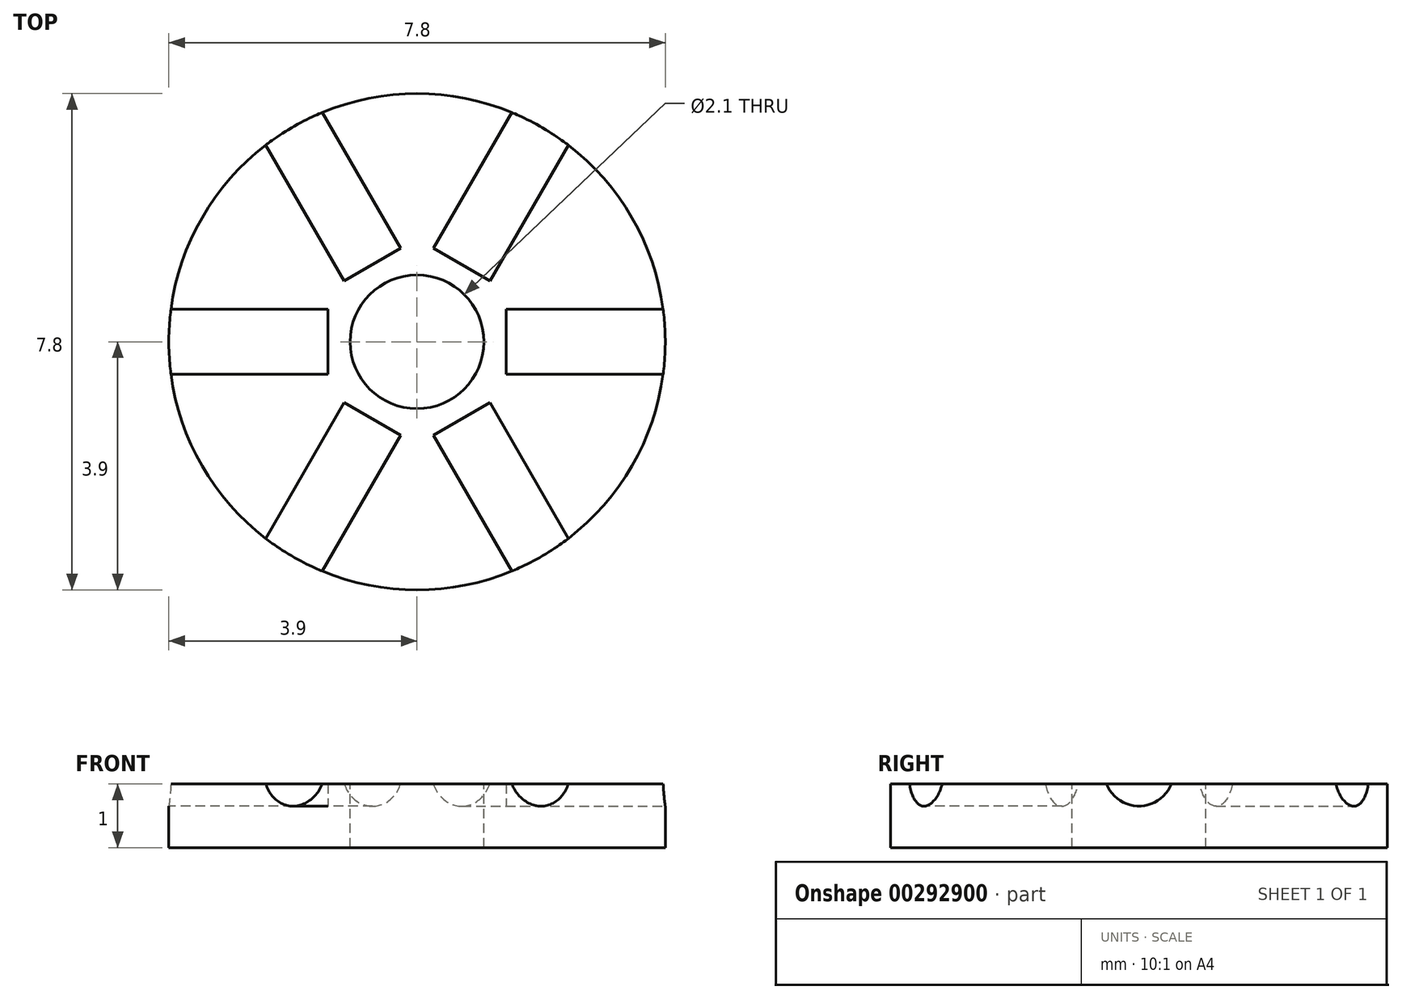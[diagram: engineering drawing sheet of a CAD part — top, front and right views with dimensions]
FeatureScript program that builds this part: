
annotation { "Feature Type Name" : "Feature", "Feature Type Description" : "" }
export const myFeature = defineFeature(function(context is Context, id is Id, definition is map)
    precondition{}
    {
        {
            var Q0;
            Q0=qCreatedBy(makeId("Top.planeOp"),FACE);
            var sketch = newSketch(context, id + "F0", { "sketchPlane" : qUnion([Q0])});
            skCircle(sketch, "E0", {"center": v(0, 0) * mm, "radius": 3.9 * mm});
            skSolve(sketch);
        }
        {
            var Q0;
            Q0=makeQuery(id+"F0.imprint","IMPRINT",FACE,{"disambiguationData":[TD([[makeQuery(id+"F0.imprint","IMPRINT",EDGE,{"derivedFrom":sQuery(id+"F0.wireOp",EDGE,"E0")}),1.0]])]});
            extrude(context, id + "F1", {"entities" : qUnion([Q0]), "depth" : 1 * mm});
        }
        {
            var Q0;
            Q0=makeQuery(id+"F1.opExtrude","CAP_FACE",FACE,{"disambiguationData":[OSD([sQuery(id+"F0.wireOp",EDGE,"E0")])],"isStart":false});
            var sketch = newSketch(context, id + "F2", { "sketchPlane" : qUnion([Q0])});
            skCircle(sketch, "E1", {"center": v(0, 0) * mm, "radius": 1.05 * mm});
            skSolve(sketch);
        }
        {
            var Q0;
            Q0=makeQuery(id+"F2.imprint","IMPRINT",FACE,{"disambiguationData":[TD([[makeQuery(id+"F2.imprint","IMPRINT",EDGE,{"derivedFrom":sQuery(id+"F2.wireOp",EDGE,"E1")}),1.0]])]});
            var Q1;
            Q1=sQuery(id+"F2.wireOp",EDGE,"E1");
            extrude(context, id + "F3", {"entities" : qUnion([Q0]), "operationType" : NewBodyOperationType.REMOVE, "surfaceEntities" : qUnion([Q1]), "oppositeDirection" : true, "depth" : 25 * mm});
        }
        {
            var Q0;
            Q0=qCreatedBy(makeId("Front.planeOp"),FACE);
            var sketch = newSketch(context, id + "F4", { "sketchPlane" : qUnion([Q0])});
            skLineSegment(sketch, "E2", {"start": v(0, 0) * mm, "end": v(0, 13.37) * mm, "construction": true});
            skSolve(sketch);
        }
        {
            var Q0;
            Q0=qCreatedBy(makeId("Right.planeOp"),FACE);
            cPlane(context, id + "F5", {"entities" : qUnion([Q0]), "cplaneType" : CPlaneType.OFFSET, "offset" : 3.9 * mm, "width" : 150 * mm, "height" : 150 * mm});
        }
        {
            var Q0;
            Q0=qCreatedBy(id+"F5.planeOp",FACE);
            var sketch = newSketch(context, id + "F6", { "sketchPlane" : qUnion([Q0])});
            skLineSegment(sketch, "E3", {"start": v(0, 0) * mm, "end": v(0, 1.2) * mm, "construction": true});
            skCircle(sketch, "E4", {"center": v(0, 1.2) * mm, "radius": 0.55 * mm});
            skSolve(sketch);
        }
        {
            var Q0;
            Q0 = qSketchRegion(id + "F6", true);
            extrude(context, id + "F7", {"entities" : qUnion([Q0]), "oppositeDirection" : true, "depth" : 2.5 * mm});
        }
        {
            var Q0;
            Q0=makeQuery(id+"F7.opExtrude","SWEPT_BODY",BODY,{"disambiguationData":[OSD([sQuery(id+"F6.wireOp",EDGE,"E4")])]});
            var Q1;
            Q1=sQuery(id+"F4.wireOp",EDGE,"E2");
            circularPattern(context, id + "F8", {"operationType" : NewBodyOperationType.REMOVE, "entities" : qUnion([Q0]), "axis" : qUnion([Q1]), "angle" : 360 * degree, "instanceCount" : 6, "equalSpace" : true});
        }
    });
